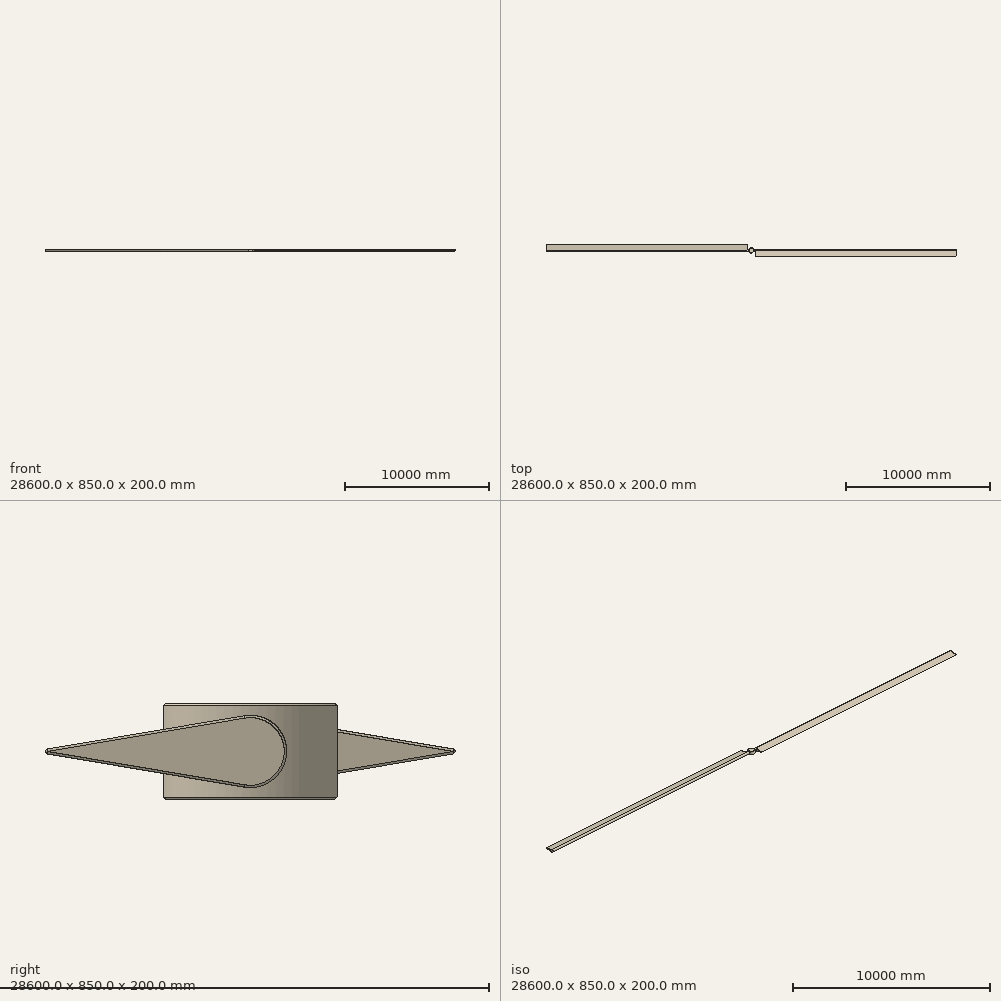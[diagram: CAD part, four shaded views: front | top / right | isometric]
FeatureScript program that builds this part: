
annotation { "Feature Type Name" : "Feature", "Feature Type Description" : "" }
export const myFeature = defineFeature(function(context is Context, id is Id, definition is map)
    precondition{}
    {
        {
            var Q0;
            Q0=qCreatedBy(makeId("Top.planeOp"),FACE);
            var sketch = newSketch(context, id + "F0", { "sketchPlane" : qUnion([Q0])});
            skCircle(sketch, "E0", {"center": v(0, 0) * mm, "radius": 180 * mm});
            skSolve(sketch);
        }
        {
            var Q0;
            Q0=makeQuery(id+"F0.imprint","IMPRINT",FACE,{"disambiguationData":[TD([[makeQuery(id+"F0.imprint","IMPRINT",EDGE,{"derivedFrom":sQuery(id+"F0.wireOp",EDGE,"E0")}),1.0]])]});
            extrude(context, id + "F1", {"entities" : qUnion([Q0]), "depth" : 200 * mm, "offsetDistance" : 25 * mm, "symmetric" : true});
        }
        {
            var Q0;
            Q0=qCreatedBy(makeId("Right.planeOp"),FACE);
            var sketch = newSketch(context, id + "F2", { "sketchPlane" : qUnion([Q0])});
            skCircle(sketch, "E1", {"center": v(0, 0) * mm, "radius": 75 * mm});
            skSolve(sketch);
        }
        {
            var Q0;
            Q0=qSketchRegion(id+"F2",true);
            extrude(context, id + "F3", {"entities" : qUnion([Q0]), "operationType" : NewBodyOperationType.ADD, "depth" : 600 * mm, "offsetDistance" : 25 * mm, "symmetric" : true});
        }
        {
            var Q0;
            Q0=makeQuery(id+"F3.opExtrude","CAP_FACE",FACE,{"disambiguationData":[OSD([sQuery(id+"F2.wireOp",EDGE,"E1")])],"isStart":true});
            var sketch = newSketch(context, id + "F4", { "sketchPlane" : qUnion([Q0])});
            skPoint(sketch, "E2", {"position": v(-450, 0) * mm});
            skLineSegment(sketch, "E3", {"start": v(-450, 0) * mm, "end": v(-12.5, 73.95) * mm});
            skLineSegment(sketch, "E4", {"start": v(-450, 0) * mm, "end": v(-12.5, -73.95) * mm});
            skSolve(sketch);
        }
        {
            var Q0;
            {var subQ0=sQuery(id+"F4.wireOp",EDGE,"E3");Q0=makeQuery(id+"F4.imprint","IMPRINT",FACE,{"disambiguationData":[TD([[makeQuery(id+"F4.imprint","IMPRINT",EDGE,{"derivedFrom":subQ0}),-1.0]])]});}
            var Q1;
            {var subQ0=makeQuery(id+"F3.opExtrude","CAP_EDGE",EDGE,{"disambiguationData":[OSD([sQuery(id+"F2.wireOp",EDGE,"E1")])],"isStart":true});var subQ1=makeQuery(id+"F4.imprint","INTERSECT",VERTEX,{"derivedFrom":[subQ0,sQuery(id+"F4.wireOp",EDGE,"E3")]});Q1=makeQuery(id+"F4.imprint","IMPRINT",FACE,{"disambiguationData":[TD([[makeQuery(id+"F4.imprint","IMPRINT",EDGE,{"disambiguationData":[TD([[subQ1,-1.0]])],"derivedFrom":subQ0}),-1.0]])]});}
            extrude(context, id + "F5", {"entities" : qUnion([Q0, Q1]), "operationType" : NewBodyOperationType.ADD, "depth" : 14000 * mm, "offsetDistance" : 25 * mm});
        }
        {
            var Q0;
            Q0=makeQuery(id+"F3.opExtrude","CAP_FACE",FACE,{"disambiguationData":[OSD([sQuery(id+"F2.wireOp",EDGE,"E1")])],"isStart":false});
            var sketch = newSketch(context, id + "F6", { "sketchPlane" : qUnion([Q0])});
            skPoint(sketch, "E5", {"position": v(-450, 0) * mm});
            skLineSegment(sketch, "E6", {"start": v(-450, 0) * mm, "end": v(-12.5, 73.95) * mm});
            skLineSegment(sketch, "E7", {"start": v(-450, 0) * mm, "end": v(-12.5, -73.95) * mm});
            skSolve(sketch);
        }
        {
            var Q0;
            Q0=qSketchRegion(id+"F6",true);
            var Q1;
            {var subQ0=makeQuery(id+"F3.opExtrude","CAP_EDGE",EDGE,{"disambiguationData":[OSD([sQuery(id+"F2.wireOp",EDGE,"E1")])],"isStart":false});var subQ1=makeQuery(id+"F6.imprint","INTERSECT",VERTEX,{"derivedFrom":[subQ0,sQuery(id+"F6.wireOp",EDGE,"E6")]});Q1=makeQuery(id+"F6.imprint","IMPRINT",FACE,{"disambiguationData":[TD([[makeQuery(id+"F6.imprint","IMPRINT",EDGE,{"disambiguationData":[TD([[subQ1,1.0]])],"derivedFrom":subQ0}),1.0]])]});}
            var Q2;
            {var subQ0=sQuery(id+"F6.wireOp",EDGE,"E6");Q2=makeQuery(id+"F6.imprint","IMPRINT",FACE,{"disambiguationData":[TD([[makeQuery(id+"F6.imprint","IMPRINT",EDGE,{"derivedFrom":subQ0}),-1.0]])]});}
            extrude(context, id + "F7", {"entities" : qUnion([Q0, Q1, Q2]), "operationType" : NewBodyOperationType.ADD, "depth" : 14000 * mm, "offsetDistance" : 25 * mm});
        }
        {
            var Q0;
            Q0=makeQuery(id+"F1.opExtrude","CAP_FACE",FACE,{"disambiguationData":[OSD([sQuery(id+"F0.wireOp",EDGE,"E0")])],"isStart":false});
            var sketch = newSketch(context, id + "F8", { "sketchPlane" : qUnion([Q0])});
            skCircle(sketch, "E8", {"center": v(0, 0) * mm, "radius": 150 * mm});
            skLineSegment(sketch, "E9", {"start": v(0, 0) * mm, "end": v(-294.15, 0) * mm, "construction": true});
            skLineSegment(sketch, "E10", {"start": v(0, 0) * mm, "end": v(-428.57, 0) * mm, "construction": true});
            skPoint(sketch, "E11", {"position": v(-150, 0) * mm});
            skPoint(sketch, "E12.1.0", {"position": v(0, -150) * mm});
            skPoint(sketch, "E12.2.0", {"position": v(150, 0) * mm});
            skPoint(sketch, "E12.3.0", {"position": v(0, 150) * mm});
            skLineSegment(sketch, "E13", {"start": v(0, 268.82) * mm, "end": v(0, -283.1) * mm, "construction": true});
            skLineSegment(sketch, "E14", {"start": v(0, 0) * mm, "end": v(383.6, 0) * mm, "construction": true});
            skCircle(sketch, "E15", {"center": v(0, -150) * mm, "radius": 15 * mm});
            skCircle(sketch, "E16.1.0", {"center": v(150, 0) * mm, "radius": 15 * mm});
            skCircle(sketch, "E16.2.0", {"center": v(0, 150) * mm, "radius": 15 * mm});
            skCircle(sketch, "E16.3.0", {"center": v(-150, 0) * mm, "radius": 15 * mm});
            skSolve(sketch);
        }
        {
            var Q0;
            Q0=sQuery(id+"F8.wireOp",VERTEX,"E11");
            var Q1;
            Q1=sQuery(id+"F8.wireOp",VERTEX,"E12.3.0");
            var Q2;
            Q2=sQuery(id+"F8.wireOp",VERTEX,"E12.2.0");
            var Q3;
            Q3=sQuery(id+"F8.wireOp",VERTEX,"E12.1.0");
            var Q4;
            Q4=makeQuery(id+"F1.opExtrude","SWEPT_BODY",BODY,{"disambiguationData":[OSD([sQuery(id+"F0.wireOp",EDGE,"E0")])]});
            hole(context, id + "F9", {"style" : HoleStyle.SIMPLE, "endStyle" : HoleEndStyle.THROUGH, "standardTappedOrClearance" : lookupTablePath({ "standard" : "ISO", "engagement" : "75%", "pitch" : "1.25 mm", "size" : "M8", "type" : "Tapped" }), "standardBlindInLast" : lookupTablePath({ "standard" : "ISO", "engagement" : "75%", "pitch" : "1.25 mm", "size" : "M8", "type" : "Tapped" }), "holeDiameter" : 6.8 * mm, "majorDiameter" : 8 * mm, "showTappedDepth" : true, "isTappedThrough" : true, "tappedDepth" : 12 * mm, "tapClearance" : 3, "locations" : qUnion([Q0, Q1, Q2, Q3]), "scope" : qUnion([Q4])});
        }
        {
            var Q0;
            Q0=makeQuery(id+"F7.opExtrude","SWEPT_EDGE",EDGE,{"disambiguationData":[OSD([sQuery(id+"F6.wireOp",EDGE,"E6"),sQuery(id+"F6.wireOp",EDGE,"E7")])]});
            var Q1;
            Q1=makeQuery(id+"F7.opExtrude","CAP_EDGE",EDGE,{"disambiguationData":[OSD([sQuery(id+"F6.wireOp",EDGE,"E6")])],"isStart":true});
            var Q2;
            Q2=makeQuery(id+"F7.opExtrude","CAP_EDGE",EDGE,{"disambiguationData":[OSD([sQuery(id+"F6.wireOp",EDGE,"E7")])],"isStart":true});
            var Q3;
            Q3=makeQuery(id+"F7.opExtrude","CAP_EDGE",EDGE,{"disambiguationData":[OSD([sQuery(id+"F6.wireOp",EDGE,"E7")])],"isStart":false});
            var Q4;
            Q4=makeQuery(id+"F7.opExtrude","CAP_EDGE",EDGE,{"disambiguationData":[OSD([sQuery(id+"F6.wireOp",EDGE,"E6")])],"isStart":false});
            var Q5;
            Q5=makeQuery(id+"F7.opExtrude","CAP_EDGE",EDGE,{"disambiguationData":[OSD([sQuery(id+"F2.wireOp",EDGE,"E1")])],"isStart":false});
            var Q6;
            Q6=makeQuery(id+"F5.opExtrude","CAP_EDGE",EDGE,{"disambiguationData":[OSD([sQuery(id+"F4.wireOp",EDGE,"E4")])],"isStart":true});
            var Q7;
            Q7=makeQuery(id+"F5.opExtrude","CAP_EDGE",EDGE,{"disambiguationData":[OSD([sQuery(id+"F4.wireOp",EDGE,"E3")])],"isStart":true});
            var Q8;
            Q8=makeQuery(id+"F5.opExtrude","SWEPT_EDGE",EDGE,{"disambiguationData":[OSD([sQuery(id+"F4.wireOp",EDGE,"E3"),sQuery(id+"F4.wireOp",EDGE,"E4")])]});
            var Q9;
            Q9=makeQuery(id+"F5.opExtrude","CAP_EDGE",EDGE,{"disambiguationData":[OSD([sQuery(id+"F2.wireOp",EDGE,"E1")])],"isStart":false});
            var Q10;
            Q10=makeQuery(id+"F5.opExtrude","CAP_EDGE",EDGE,{"disambiguationData":[OSD([sQuery(id+"F4.wireOp",EDGE,"E4")])],"isStart":false});
            var Q11;
            Q11=makeQuery(id+"F5.opExtrude","CAP_EDGE",EDGE,{"disambiguationData":[OSD([sQuery(id+"F4.wireOp",EDGE,"E3")])],"isStart":false});
            fillet(context, id + "F10", {"entities" : qUnion([Q0, Q1, Q2, Q3, Q4, Q5, Q6, Q7, Q8, Q9, Q10, Q11]), "radius" : 5 * mm, "tangentPropagation" : true, "allowEdgeOverflow" : false});
        }
        {
            var Q0;
            Q0=makeQuery(id+"F1.opExtrude","CAP_EDGE",EDGE,{"disambiguationData":[OSD([sQuery(id+"F0.wireOp",EDGE,"E0")])],"isStart":false});
            var Q1;
            Q1=makeQuery(id+"F1.opExtrude","CAP_EDGE",EDGE,{"disambiguationData":[OSD([sQuery(id+"F0.wireOp",EDGE,"E0")])],"isStart":true});
            chamfer(context, id + "F11", {"entities" : qUnion([Q0, Q1]), "width" : 5 * mm, "tangentPropagation" : true});
        }
        {
            var Q0;
            Q0=qCreatedBy(makeId("Front.planeOp"),FACE);
            cPlane(context, id + "F12", {"entities" : qUnion([Q0]), "cplaneType" : CPlaneType.OFFSET, "offset" : 150 * mm, "width" : 150 * mm, "height" : 150 * mm});
        }
        {
            var Q0;
            Q0=qCreatedBy(id+"F12.planeOp",FACE);
            var sketch = newSketch(context, id + "F13", { "sketchPlane" : qUnion([Q0])});
            skLineSegment(sketch, "E17", {"start": v(0, 0) * mm, "end": v(0, 200) * mm, "construction": true});
            skLineSegment(sketch, "E18.bottom", {"start": v(5, 100) * mm, "end": v(-5, 100) * mm});
            skLineSegment(sketch, "E18.top", {"start": v(5, 95) * mm, "end": v(-5, 95) * mm});
            skLineSegment(sketch, "E18.left", {"start": v(5, 100) * mm, "end": v(5, 95) * mm});
            skLineSegment(sketch, "E18.right", {"start": v(-5, 100) * mm, "end": v(-5, 95) * mm});
            skPoint(sketch, "E18.middle", {"position": v(0, 97.5) * mm});
            skPoint(sketch, "E19", {"position": v(0, 100) * mm});
            skLineSegment(sketch, "E20.bottom", {"start": v(5, -100) * mm, "end": v(-5, -100) * mm});
            skLineSegment(sketch, "E20.top", {"start": v(5, -95) * mm, "end": v(-5, -95) * mm});
            skLineSegment(sketch, "E20.left", {"start": v(5, -100) * mm, "end": v(5, -95) * mm});
            skLineSegment(sketch, "E20.right", {"start": v(-5, -100) * mm, "end": v(-5, -95) * mm});
            skPoint(sketch, "E20.middle", {"position": v(0, -97.5) * mm});
            skSolve(sketch);
        }
        {
            var Q0;
            Q0=qSketchRegion(id+"F13",true);
            extrude(context, id + "F14", {"entities" : qUnion([Q0]), "operationType" : NewBodyOperationType.REMOVE, "oppositeDirection" : true, "depth" : 40 * mm, "offsetDistance" : 25 * mm, "symmetric" : true});
        }
        {
            var Q0;
            {var subQ0=sQuery(id+"F8.wireOp",EDGE,"E15");var subQ1=sQuery(id+"F8.wireOp",EDGE,"E8");var subQ2=makeQuery(id+"F8.imprint","INTERSECT",VERTEX,{"disambiguationData":[OD(0.0)],"derivedFrom":[subQ1,subQ0]});Q0=makeQuery(id+"F8.imprint","IMPRINT",FACE,{"disambiguationData":[TD([[makeQuery(id+"F8.imprint","IMPRINT",EDGE,{"disambiguationData":[TD([[subQ2,-1.0]])],"derivedFrom":subQ1}),1.0]])]});}
            var Q1;
            {var subQ0=sQuery(id+"F8.wireOp",EDGE,"E15");var subQ1=sQuery(id+"F8.wireOp",EDGE,"E8");var subQ2=makeQuery(id+"F8.imprint","INTERSECT",VERTEX,{"disambiguationData":[OD(0.0)],"derivedFrom":[subQ1,subQ0]});Q1=makeQuery(id+"F8.imprint","IMPRINT",FACE,{"disambiguationData":[TD([[makeQuery(id+"F8.imprint","IMPRINT",EDGE,{"disambiguationData":[TD([[subQ2,-1.0]])],"derivedFrom":subQ1}),-1.0]])]});}
            extrude(context, id + "F15", {"entities" : qUnion([Q0, Q1]), "operationType" : NewBodyOperationType.REMOVE, "oppositeDirection" : true, "depth" : 5 * mm, "offsetDistance" : 25 * mm});
        }
        {
            var Q0;
            {var subQ0=sQuery(id+"F8.wireOp",EDGE,"E16.3.0");var subQ1=sQuery(id+"F8.wireOp",EDGE,"E8");var subQ2=makeQuery(id+"F8.imprint","INTERSECT",VERTEX,{"disambiguationData":[OD(0.0)],"derivedFrom":[subQ1,subQ0]});Q0=makeQuery(id+"F8.imprint","IMPRINT",FACE,{"disambiguationData":[TD([[makeQuery(id+"F8.imprint","IMPRINT",EDGE,{"disambiguationData":[TD([[subQ2,-1.0]])],"derivedFrom":subQ1}),-1.0]])]});}
            var Q1;
            {var subQ0=sQuery(id+"F8.wireOp",EDGE,"E16.3.0");var subQ1=sQuery(id+"F8.wireOp",EDGE,"E8");var subQ2=makeQuery(id+"F8.imprint","INTERSECT",VERTEX,{"disambiguationData":[OD(0.0)],"derivedFrom":[subQ1,subQ0]});Q1=makeQuery(id+"F8.imprint","IMPRINT",FACE,{"disambiguationData":[TD([[makeQuery(id+"F8.imprint","IMPRINT",EDGE,{"disambiguationData":[TD([[subQ2,-1.0]])],"derivedFrom":subQ1}),1.0]])]});}
            var Q2;
            {var subQ0=sQuery(id+"F8.wireOp",EDGE,"E16.2.0");var subQ1=sQuery(id+"F8.wireOp",EDGE,"E8");var subQ2=makeQuery(id+"F8.imprint","INTERSECT",VERTEX,{"disambiguationData":[OD(0.0)],"derivedFrom":[subQ1,subQ0]});Q2=makeQuery(id+"F8.imprint","IMPRINT",FACE,{"disambiguationData":[TD([[makeQuery(id+"F8.imprint","IMPRINT",EDGE,{"disambiguationData":[TD([[subQ2,-1.0]])],"derivedFrom":subQ1}),1.0]])]});}
            var Q3;
            {var subQ0=sQuery(id+"F8.wireOp",EDGE,"E16.2.0");var subQ1=sQuery(id+"F8.wireOp",EDGE,"E8");var subQ2=makeQuery(id+"F8.imprint","INTERSECT",VERTEX,{"disambiguationData":[OD(0.0)],"derivedFrom":[subQ1,subQ0]});Q3=makeQuery(id+"F8.imprint","IMPRINT",FACE,{"disambiguationData":[TD([[makeQuery(id+"F8.imprint","IMPRINT",EDGE,{"disambiguationData":[TD([[subQ2,-1.0]])],"derivedFrom":subQ1}),-1.0]])]});}
            var Q4;
            {var subQ0=sQuery(id+"F8.wireOp",EDGE,"E16.1.0");var subQ1=sQuery(id+"F8.wireOp",EDGE,"E8");var subQ2=makeQuery(id+"F8.imprint","INTERSECT",VERTEX,{"disambiguationData":[OD(0.0)],"derivedFrom":[subQ1,subQ0]});Q4=makeQuery(id+"F8.imprint","IMPRINT",FACE,{"disambiguationData":[TD([[makeQuery(id+"F8.imprint","IMPRINT",EDGE,{"disambiguationData":[TD([[subQ2,1.0]])],"derivedFrom":subQ1}),1.0]])]});}
            var Q5;
            {var subQ0=sQuery(id+"F8.wireOp",EDGE,"E16.1.0");var subQ1=sQuery(id+"F8.wireOp",EDGE,"E8");var subQ2=makeQuery(id+"F8.imprint","INTERSECT",VERTEX,{"disambiguationData":[OD(0.0)],"derivedFrom":[subQ1,subQ0]});Q5=makeQuery(id+"F8.imprint","IMPRINT",FACE,{"disambiguationData":[TD([[makeQuery(id+"F8.imprint","IMPRINT",EDGE,{"disambiguationData":[TD([[subQ2,1.0]])],"derivedFrom":subQ1}),-1.0]])]});}
            extrude(context, id + "F16", {"entities" : qUnion([Q0, Q1, Q2, Q3, Q4, Q5]), "operationType" : NewBodyOperationType.REMOVE, "oppositeDirection" : true, "depth" : 5 * mm, "offsetDistance" : 25 * mm});
        }
        {
            var Q0;
            Q0=qCreatedBy(makeId("Front.planeOp"),FACE);
            cPlane(context, id + "F17", {"entities" : qUnion([Q0]), "cplaneType" : CPlaneType.OFFSET, "offset" : 150 * mm, "oppositeDirection" : true, "width" : 150 * mm, "height" : 150 * mm});
        }
        {
            var Q0;
            Q0=qCreatedBy(id+"F17.planeOp",FACE);
            var sketch = newSketch(context, id + "F18", { "sketchPlane" : qUnion([Q0])});
            skLineSegment(sketch, "E21.bottom", {"start": v(5, 100) * mm, "end": v(-5, 100) * mm});
            skLineSegment(sketch, "E21.top", {"start": v(5, 95) * mm, "end": v(-5, 95) * mm});
            skLineSegment(sketch, "E21.left", {"start": v(5, 100) * mm, "end": v(5, 95) * mm});
            skLineSegment(sketch, "E21.right", {"start": v(-5, 100) * mm, "end": v(-5, 95) * mm});
            skPoint(sketch, "E21.middle", {"position": v(0, 97.5) * mm});
            skLineSegment(sketch, "E22", {"start": v(0, 0) * mm, "end": v(0, 133.04) * mm, "construction": true});
            skPoint(sketch, "E23", {"position": v(0, 100) * mm});
            skLineSegment(sketch, "E24.bottom", {"start": v(5, -100) * mm, "end": v(-5, -100) * mm});
            skLineSegment(sketch, "E24.top", {"start": v(5, -95) * mm, "end": v(-5, -95) * mm});
            skLineSegment(sketch, "E24.left", {"start": v(5, -100) * mm, "end": v(5, -95) * mm});
            skLineSegment(sketch, "E24.right", {"start": v(-5, -100) * mm, "end": v(-5, -95) * mm});
            skPoint(sketch, "E24.middle", {"position": v(0, -97.5) * mm});
            skSolve(sketch);
        }
        {
            var Q0;
            Q0=qSketchRegion(id+"F18",true);
            extrude(context, id + "F19", {"entities" : qUnion([Q0]), "operationType" : NewBodyOperationType.REMOVE, "oppositeDirection" : true, "depth" : 40 * mm, "offsetDistance" : 25 * mm, "symmetric" : true});
        }
        {
            var Q0;
            Q0=qCreatedBy(makeId("Right.planeOp"),FACE);
            cPlane(context, id + "F20", {"entities" : qUnion([Q0]), "cplaneType" : CPlaneType.OFFSET, "offset" : 150 * mm, "width" : 150 * mm, "height" : 150 * mm});
        }
        {
            var Q0;
            Q0=qCreatedBy(id+"F20.planeOp",FACE);
            var sketch = newSketch(context, id + "F21", { "sketchPlane" : qUnion([Q0])});
            skLineSegment(sketch, "E25", {"start": v(0, -97.5) * mm, "end": v(0, 182.32) * mm, "construction": true});
            skPoint(sketch, "E26", {"position": v(0, 100) * mm});
            skLineSegment(sketch, "E27.bottom", {"start": v(-5, 100) * mm, "end": v(5, 100) * mm});
            skLineSegment(sketch, "E27.top", {"start": v(-5, 95) * mm, "end": v(5, 95) * mm});
            skLineSegment(sketch, "E27.left", {"start": v(-5, 100) * mm, "end": v(-5, 95) * mm});
            skLineSegment(sketch, "E27.right", {"start": v(5, 100) * mm, "end": v(5, 95) * mm});
            skPoint(sketch, "E27.middle", {"position": v(0, 97.5) * mm});
            skLineSegment(sketch, "E28.bottom", {"start": v(5, -95) * mm, "end": v(-5, -95) * mm});
            skLineSegment(sketch, "E28.top", {"start": v(5, -100) * mm, "end": v(-5, -100) * mm});
            skLineSegment(sketch, "E28.left", {"start": v(5, -95) * mm, "end": v(5, -100) * mm});
            skLineSegment(sketch, "E28.right", {"start": v(-5, -95) * mm, "end": v(-5, -100) * mm});
            skPoint(sketch, "E28.middle", {"position": v(0, -97.5) * mm});
            skSolve(sketch);
        }
        {
            var Q0;
            Q0=qSketchRegion(id+"F21",true);
            extrude(context, id + "F22", {"entities" : qUnion([Q0]), "operationType" : NewBodyOperationType.REMOVE, "oppositeDirection" : true, "depth" : 40 * mm, "offsetDistance" : 25 * mm, "symmetric" : true});
        }
        {
            var Q0;
            Q0=qCreatedBy(makeId("Right.planeOp"),FACE);
            cPlane(context, id + "F23", {"entities" : qUnion([Q0]), "cplaneType" : CPlaneType.OFFSET, "offset" : 150 * mm, "oppositeDirection" : true, "width" : 150 * mm, "height" : 150 * mm});
        }
        {
            var Q0;
            Q0=qCreatedBy(id+"F23.planeOp",FACE);
            var sketch = newSketch(context, id + "F24", { "sketchPlane" : qUnion([Q0])});
            skLineSegment(sketch, "E29", {"start": v(0, 0) * mm, "end": v(0, 200) * mm, "construction": true});
            skPoint(sketch, "E30", {"position": v(0, 100) * mm});
            skLineSegment(sketch, "E31.bottom", {"start": v(-5, 95) * mm, "end": v(5, 95) * mm});
            skLineSegment(sketch, "E31.top", {"start": v(-5, 100) * mm, "end": v(5, 100) * mm});
            skLineSegment(sketch, "E31.left", {"start": v(-5, 95) * mm, "end": v(-5, 100) * mm});
            skLineSegment(sketch, "E31.right", {"start": v(5, 95) * mm, "end": v(5, 100) * mm});
            skPoint(sketch, "E31.middle", {"position": v(0, 97.5) * mm});
            skLineSegment(sketch, "E32.bottom", {"start": v(5, -100) * mm, "end": v(-5, -100) * mm});
            skLineSegment(sketch, "E32.top", {"start": v(5, -95) * mm, "end": v(-5, -95) * mm});
            skLineSegment(sketch, "E32.left", {"start": v(5, -100) * mm, "end": v(5, -95) * mm});
            skLineSegment(sketch, "E32.right", {"start": v(-5, -100) * mm, "end": v(-5, -95) * mm});
            skPoint(sketch, "E32.middle", {"position": v(0, -97.5) * mm});
            skSolve(sketch);
        }
        {
            var Q0;
            Q0=qSketchRegion(id+"F24",true);
            extrude(context, id + "F25", {"entities" : qUnion([Q0]), "operationType" : NewBodyOperationType.REMOVE, "oppositeDirection" : true, "depth" : 40 * mm, "offsetDistance" : 25 * mm, "symmetric" : true});
        }
        {
            var Q0;
            Q0=qSketchRegion(id+"F21",true);
            extrude(context, id + "F26", {"entities" : qUnion([Q0]), "operationType" : NewBodyOperationType.REMOVE, "oppositeDirection" : true, "depth" : 40 * mm, "offsetDistance" : 25 * mm, "symmetric" : true});
        }
        {
            var Q0;
            Q0=qSketchRegion(id+"F24",true);
            extrude(context, id + "F27", {"entities" : qUnion([Q0]), "operationType" : NewBodyOperationType.REMOVE, "oppositeDirection" : true, "depth" : 40 * mm, "offsetDistance" : 25 * mm, "symmetric" : true});
        }
        {
            var Q0;
            Q0=qSketchRegion(id+"F18",true);
            extrude(context, id + "F28", {"entities" : qUnion([Q0]), "operationType" : NewBodyOperationType.REMOVE, "oppositeDirection" : true, "depth" : 40 * mm, "offsetDistance" : 25 * mm, "symmetric" : true});
        }
        {
            var Q0;
            Q0=qSketchRegion(id+"F13",true);
            extrude(context, id + "F29", {"entities" : qUnion([Q0]), "operationType" : NewBodyOperationType.REMOVE, "oppositeDirection" : true, "depth" : 40 * mm, "offsetDistance" : 25 * mm, "symmetric" : true});
        }
        {
            var Q0;
            Q0=makeQuery(id+"F1.opExtrude","CAP_FACE",FACE,{"disambiguationData":[OSD([sQuery(id+"F0.wireOp",EDGE,"E0")])],"isStart":true});
            var sketch = newSketch(context, id + "F30", { "sketchPlane" : qUnion([Q0])});
            skCircle(sketch, "E33", {"center": v(0, 0) * mm, "radius": 150 * mm});
            skCircle(sketch, "E34", {"center": v(150, 0) * mm, "radius": 15 * mm});
            skPoint(sketch, "E34.centerSnap0", {"position": v(130, 0) * mm});
            skCircle(sketch, "E35.1.0", {"center": v(0, 150) * mm, "radius": 15 * mm});
            skCircle(sketch, "E35.2.0", {"center": v(-150, 0) * mm, "radius": 15 * mm});
            skCircle(sketch, "E35.3.0", {"center": v(0, -150) * mm, "radius": 15 * mm});
            skSolve(sketch);
        }
        {
            var Q0;
            {var subQ0=sQuery(id+"F30.wireOp",EDGE,"E34");var subQ1=sQuery(id+"F30.wireOp",EDGE,"E33");var subQ2=makeQuery(id+"F30.imprint","INTERSECT",VERTEX,{"disambiguationData":[OD(0.0)],"derivedFrom":[subQ1,subQ0]});Q0=makeQuery(id+"F30.imprint","IMPRINT",FACE,{"disambiguationData":[TD([[makeQuery(id+"F30.imprint","IMPRINT",EDGE,{"disambiguationData":[TD([[subQ2,1.0]])],"derivedFrom":subQ1}),1.0]])]});}
            var Q1;
            {var subQ0=sQuery(id+"F30.wireOp",EDGE,"E34");var subQ1=sQuery(id+"F30.wireOp",EDGE,"E33");var subQ2=makeQuery(id+"F30.imprint","INTERSECT",VERTEX,{"disambiguationData":[OD(0.0)],"derivedFrom":[subQ1,subQ0]});Q1=makeQuery(id+"F30.imprint","IMPRINT",FACE,{"disambiguationData":[TD([[makeQuery(id+"F30.imprint","IMPRINT",EDGE,{"disambiguationData":[TD([[subQ2,1.0]])],"derivedFrom":subQ1}),-1.0]])]});}
            var Q2;
            {var subQ0=sQuery(id+"F30.wireOp",EDGE,"E34");var subQ1=sQuery(id+"F30.wireOp",EDGE,"E33");var subQ2=makeQuery(id+"F30.imprint","INTERSECT",VERTEX,{"disambiguationData":[OD(1.0)],"derivedFrom":[subQ1,subQ0]});Q2=makeQuery(id+"F30.imprint","IMPRINT",FACE,{"disambiguationData":[TD([[makeQuery(id+"F30.imprint","IMPRINT",EDGE,{"disambiguationData":[TD([[subQ2,-1.0]])],"derivedFrom":subQ1}),-1.0]])]});}
            var Q3;
            {var subQ0=sQuery(id+"F30.wireOp",EDGE,"E34");var subQ1=sQuery(id+"F30.wireOp",EDGE,"E33");var subQ2=makeQuery(id+"F30.imprint","INTERSECT",VERTEX,{"disambiguationData":[OD(1.0)],"derivedFrom":[subQ1,subQ0]});Q3=makeQuery(id+"F30.imprint","IMPRINT",FACE,{"disambiguationData":[TD([[makeQuery(id+"F30.imprint","IMPRINT",EDGE,{"disambiguationData":[TD([[subQ2,-1.0]])],"derivedFrom":subQ1}),1.0]])]});}
            var Q4;
            {var subQ0=sQuery(id+"F30.wireOp",EDGE,"E35.1.0");var subQ1=sQuery(id+"F30.wireOp",EDGE,"E33");var subQ2=makeQuery(id+"F30.imprint","INTERSECT",VERTEX,{"disambiguationData":[OD(0.0)],"derivedFrom":[subQ1,subQ0]});Q4=makeQuery(id+"F30.imprint","IMPRINT",FACE,{"disambiguationData":[TD([[makeQuery(id+"F30.imprint","IMPRINT",EDGE,{"disambiguationData":[TD([[subQ2,-1.0]])],"derivedFrom":subQ1}),1.0]])]});}
            var Q5;
            {var subQ0=sQuery(id+"F30.wireOp",EDGE,"E35.1.0");var subQ1=sQuery(id+"F30.wireOp",EDGE,"E33");var subQ2=makeQuery(id+"F30.imprint","INTERSECT",VERTEX,{"disambiguationData":[OD(0.0)],"derivedFrom":[subQ1,subQ0]});Q5=makeQuery(id+"F30.imprint","IMPRINT",FACE,{"disambiguationData":[TD([[makeQuery(id+"F30.imprint","IMPRINT",EDGE,{"disambiguationData":[TD([[subQ2,-1.0]])],"derivedFrom":subQ1}),-1.0]])]});}
            var Q6;
            {var subQ0=sQuery(id+"F30.wireOp",EDGE,"E35.1.0");var subQ1=sQuery(id+"F30.wireOp",EDGE,"E33");var subQ2=makeQuery(id+"F30.imprint","INTERSECT",VERTEX,{"disambiguationData":[OD(1.0)],"derivedFrom":[subQ1,subQ0]});Q6=makeQuery(id+"F30.imprint","IMPRINT",FACE,{"disambiguationData":[TD([[makeQuery(id+"F30.imprint","IMPRINT",EDGE,{"disambiguationData":[TD([[subQ2,1.0]])],"derivedFrom":subQ1}),-1.0]])]});}
            var Q7;
            {var subQ0=sQuery(id+"F30.wireOp",EDGE,"E35.1.0");var subQ1=sQuery(id+"F30.wireOp",EDGE,"E33");var subQ2=makeQuery(id+"F30.imprint","INTERSECT",VERTEX,{"disambiguationData":[OD(1.0)],"derivedFrom":[subQ1,subQ0]});Q7=makeQuery(id+"F30.imprint","IMPRINT",FACE,{"disambiguationData":[TD([[makeQuery(id+"F30.imprint","IMPRINT",EDGE,{"disambiguationData":[TD([[subQ2,1.0]])],"derivedFrom":subQ1}),1.0]])]});}
            var Q8;
            {var subQ0=sQuery(id+"F30.wireOp",EDGE,"E35.3.0");var subQ1=sQuery(id+"F30.wireOp",EDGE,"E33");var subQ2=makeQuery(id+"F30.imprint","INTERSECT",VERTEX,{"disambiguationData":[OD(1.0)],"derivedFrom":[subQ1,subQ0]});Q8=makeQuery(id+"F30.imprint","IMPRINT",FACE,{"disambiguationData":[TD([[makeQuery(id+"F30.imprint","IMPRINT",EDGE,{"disambiguationData":[TD([[subQ2,1.0]])],"derivedFrom":subQ1}),1.0]])]});}
            var Q9;
            {var subQ0=sQuery(id+"F30.wireOp",EDGE,"E35.3.0");var subQ1=sQuery(id+"F30.wireOp",EDGE,"E33");var subQ2=makeQuery(id+"F30.imprint","INTERSECT",VERTEX,{"disambiguationData":[OD(1.0)],"derivedFrom":[subQ1,subQ0]});Q9=makeQuery(id+"F30.imprint","IMPRINT",FACE,{"disambiguationData":[TD([[makeQuery(id+"F30.imprint","IMPRINT",EDGE,{"disambiguationData":[TD([[subQ2,1.0]])],"derivedFrom":subQ1}),-1.0]])]});}
            var Q10;
            {var subQ0=sQuery(id+"F30.wireOp",EDGE,"E35.3.0");var subQ1=sQuery(id+"F30.wireOp",EDGE,"E33");var subQ2=makeQuery(id+"F30.imprint","INTERSECT",VERTEX,{"disambiguationData":[OD(0.0)],"derivedFrom":[subQ1,subQ0]});Q10=makeQuery(id+"F30.imprint","IMPRINT",FACE,{"disambiguationData":[TD([[makeQuery(id+"F30.imprint","IMPRINT",EDGE,{"disambiguationData":[TD([[subQ2,-1.0]])],"derivedFrom":subQ1}),-1.0]])]});}
            var Q11;
            {var subQ0=sQuery(id+"F30.wireOp",EDGE,"E35.3.0");var subQ1=sQuery(id+"F30.wireOp",EDGE,"E33");var subQ2=makeQuery(id+"F30.imprint","INTERSECT",VERTEX,{"disambiguationData":[OD(0.0)],"derivedFrom":[subQ1,subQ0]});Q11=makeQuery(id+"F30.imprint","IMPRINT",FACE,{"disambiguationData":[TD([[makeQuery(id+"F30.imprint","IMPRINT",EDGE,{"disambiguationData":[TD([[subQ2,-1.0]])],"derivedFrom":subQ1}),1.0]])]});}
            var Q12;
            {var subQ0=sQuery(id+"F30.wireOp",EDGE,"E35.2.0");var subQ1=sQuery(id+"F30.wireOp",EDGE,"E33");var subQ2=makeQuery(id+"F30.imprint","INTERSECT",VERTEX,{"disambiguationData":[OD(1.0)],"derivedFrom":[subQ1,subQ0]});Q12=makeQuery(id+"F30.imprint","IMPRINT",FACE,{"disambiguationData":[TD([[makeQuery(id+"F30.imprint","IMPRINT",EDGE,{"disambiguationData":[TD([[subQ2,1.0]])],"derivedFrom":subQ1}),1.0]])]});}
            var Q13;
            {var subQ0=sQuery(id+"F30.wireOp",EDGE,"E35.2.0");var subQ1=sQuery(id+"F30.wireOp",EDGE,"E33");var subQ2=makeQuery(id+"F30.imprint","INTERSECT",VERTEX,{"disambiguationData":[OD(1.0)],"derivedFrom":[subQ1,subQ0]});Q13=makeQuery(id+"F30.imprint","IMPRINT",FACE,{"disambiguationData":[TD([[makeQuery(id+"F30.imprint","IMPRINT",EDGE,{"disambiguationData":[TD([[subQ2,1.0]])],"derivedFrom":subQ1}),-1.0]])]});}
            var Q14;
            {var subQ0=sQuery(id+"F30.wireOp",EDGE,"E35.2.0");var subQ1=sQuery(id+"F30.wireOp",EDGE,"E33");var subQ2=makeQuery(id+"F30.imprint","INTERSECT",VERTEX,{"disambiguationData":[OD(0.0)],"derivedFrom":[subQ1,subQ0]});Q14=makeQuery(id+"F30.imprint","IMPRINT",FACE,{"disambiguationData":[TD([[makeQuery(id+"F30.imprint","IMPRINT",EDGE,{"disambiguationData":[TD([[subQ2,-1.0]])],"derivedFrom":subQ1}),-1.0]])]});}
            var Q15;
            {var subQ0=sQuery(id+"F30.wireOp",EDGE,"E35.2.0");var subQ1=sQuery(id+"F30.wireOp",EDGE,"E33");var subQ2=makeQuery(id+"F30.imprint","INTERSECT",VERTEX,{"disambiguationData":[OD(0.0)],"derivedFrom":[subQ1,subQ0]});Q15=makeQuery(id+"F30.imprint","IMPRINT",FACE,{"disambiguationData":[TD([[makeQuery(id+"F30.imprint","IMPRINT",EDGE,{"disambiguationData":[TD([[subQ2,-1.0]])],"derivedFrom":subQ1}),1.0]])]});}
            extrude(context, id + "F31", {"entities" : qUnion([Q0, Q1, Q2, Q3, Q4, Q5, Q6, Q7, Q8, Q9, Q10, Q11, Q12, Q13, Q14, Q15]), "operationType" : NewBodyOperationType.REMOVE, "oppositeDirection" : true, "depth" : 5 * mm, "offsetDistance" : 25 * mm});
        }
    });
